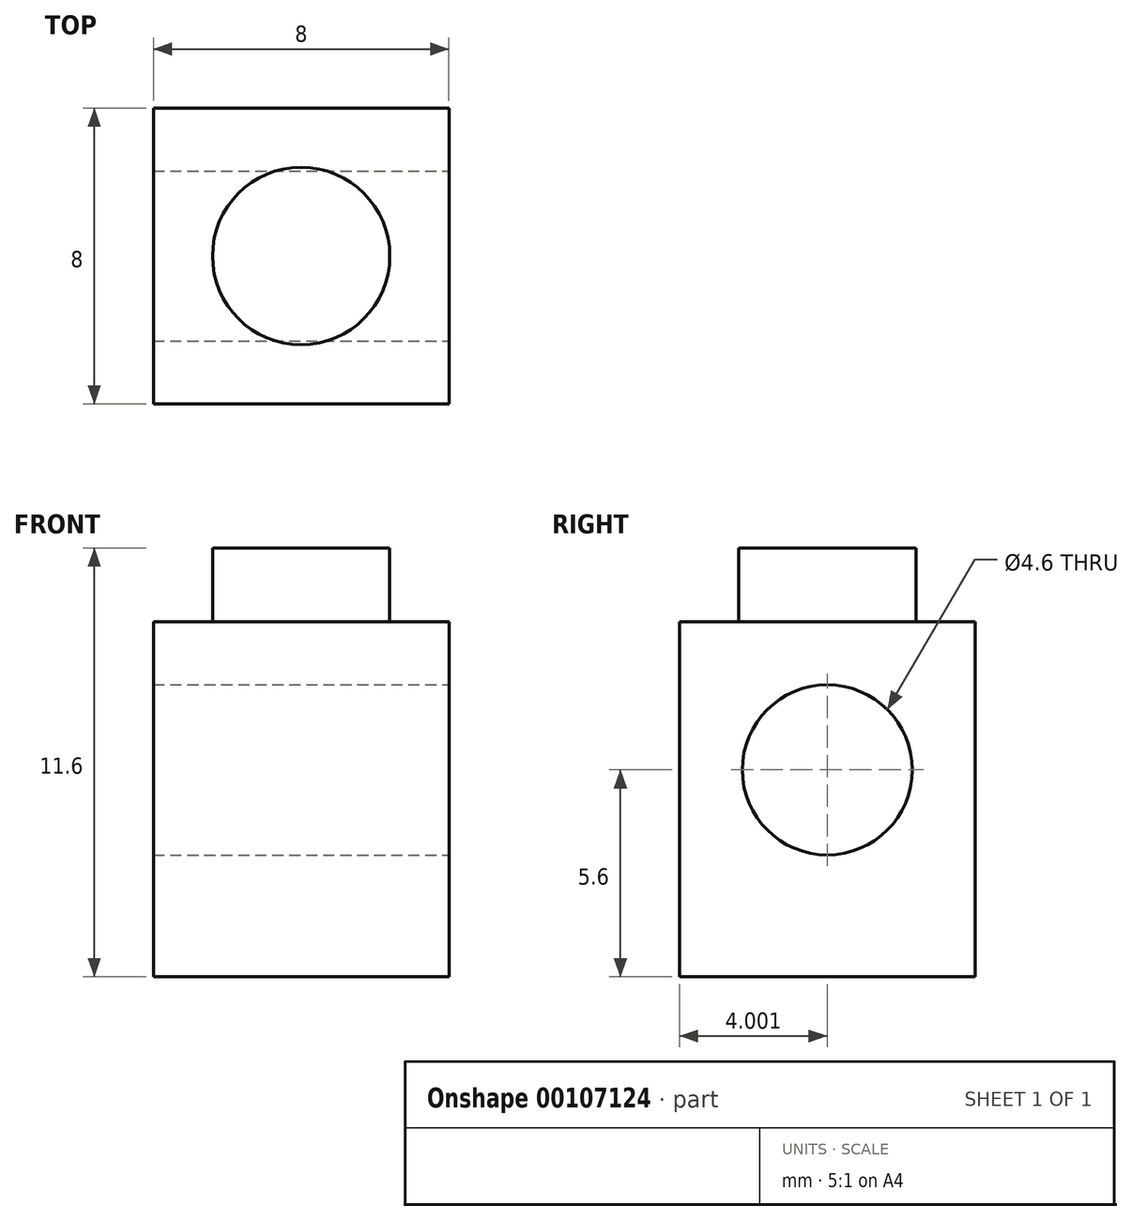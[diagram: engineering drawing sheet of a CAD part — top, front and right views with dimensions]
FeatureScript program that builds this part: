
annotation { "Feature Type Name" : "Feature", "Feature Type Description" : "" }
export const myFeature = defineFeature(function(context is Context, id is Id, definition is map)
    precondition{}
    {
        {
            var Q0;
            Q0=qCreatedBy(makeId("Top.planeOp"),FACE);
            var sketch = newSketch(context, id + "F0", { "sketchPlane" : qUnion([Q0])});
            skLineSegment(sketch, "E0.bottom", {"start": v(-34.09, 23.3) * mm, "end": v(-42.09, 23.3) * mm});
            skLineSegment(sketch, "E0.top", {"start": v(-34.09, 31.3) * mm, "end": v(-42.09, 31.3) * mm});
            skLineSegment(sketch, "E0.left", {"start": v(-34.09, 23.3) * mm, "end": v(-34.09, 31.3) * mm});
            skLineSegment(sketch, "E0.right", {"start": v(-42.09, 23.3) * mm, "end": v(-42.09, 31.3) * mm});
            skPoint(sketch, "E0.middle", {"position": v(-38.09, 27.3) * mm});
            skSolve(sketch);
        }
        {
            var Q0;
            Q0=makeQuery(id+"F0.imprint","IMPRINT",FACE,{"disambiguationData":[TD([[makeQuery(id+"F0.imprint","IMPRINT",EDGE,{"derivedFrom":sQuery(id+"F0.wireOp",EDGE,"E0.bottom")}),-1.0]])]});
            extrude(context, id + "F1", {"entities" : qUnion([Q0]), "depth" : 9.6 * mm});
        }
        {
            var Q0;
            Q0=makeQuery(id+"F1.opExtrude","SWEPT_FACE",FACE,{"disambiguationData":[OSD([sQuery(id+"F0.wireOp",EDGE,"E0.left")])]});
            var sketch = newSketch(context, id + "F2", { "sketchPlane" : qUnion([Q0])});
            skLineSegment(sketch, "E1", {"start": v(27.3, 0) * mm, "end": v(27.3, 5.6) * mm, "construction": true});
            skCircle(sketch, "E2", {"center": v(27.3, 5.6) * mm, "radius": 2.3 * mm});
            skSolve(sketch);
        }
        {
            var Q0;
            Q0=makeQuery(id+"F2.imprint","IMPRINT",FACE,{"disambiguationData":[TD([[makeQuery(id+"F2.imprint","IMPRINT",EDGE,{"derivedFrom":sQuery(id+"F2.wireOp",EDGE,"E2")}),1.0]])]});
            extrude(context, id + "F3", {"entities" : qUnion([Q0]), "operationType" : NewBodyOperationType.REMOVE, "oppositeDirection" : true, "depth" : 25 * mm});
        }
        {
            var Q0;
            Q0=makeQuery(id+"F1.opExtrude","CAP_FACE",FACE,{"disambiguationData":[OSD([sQuery(id+"F0.wireOp",EDGE,"E0.bottom"),sQuery(id+"F0.wireOp",EDGE,"E0.top"),sQuery(id+"F0.wireOp",EDGE,"E0.left"),sQuery(id+"F0.wireOp",EDGE,"E0.right")])],"isStart":false});
            var sketch = newSketch(context, id + "F4", { "sketchPlane" : qUnion([Q0])});
            skLineSegment(sketch, "E3", {"start": v(-34.09, 27.3) * mm, "end": v(-38.09, 27.3) * mm, "construction": true});
            skCircle(sketch, "E4", {"center": v(-38.09, 27.3) * mm, "radius": 2.4 * mm});
            skSolve(sketch);
        }
        {
            var Q0;
            Q0=makeQuery(id+"F4.imprint","IMPRINT",FACE,{"disambiguationData":[TD([[makeQuery(id+"F4.imprint","IMPRINT",EDGE,{"derivedFrom":sQuery(id+"F4.wireOp",EDGE,"E4")}),1.0]])]});
            extrude(context, id + "F5", {"entities" : qUnion([Q0]), "operationType" : NewBodyOperationType.ADD, "depth" : 2 * mm});
        }
    });
